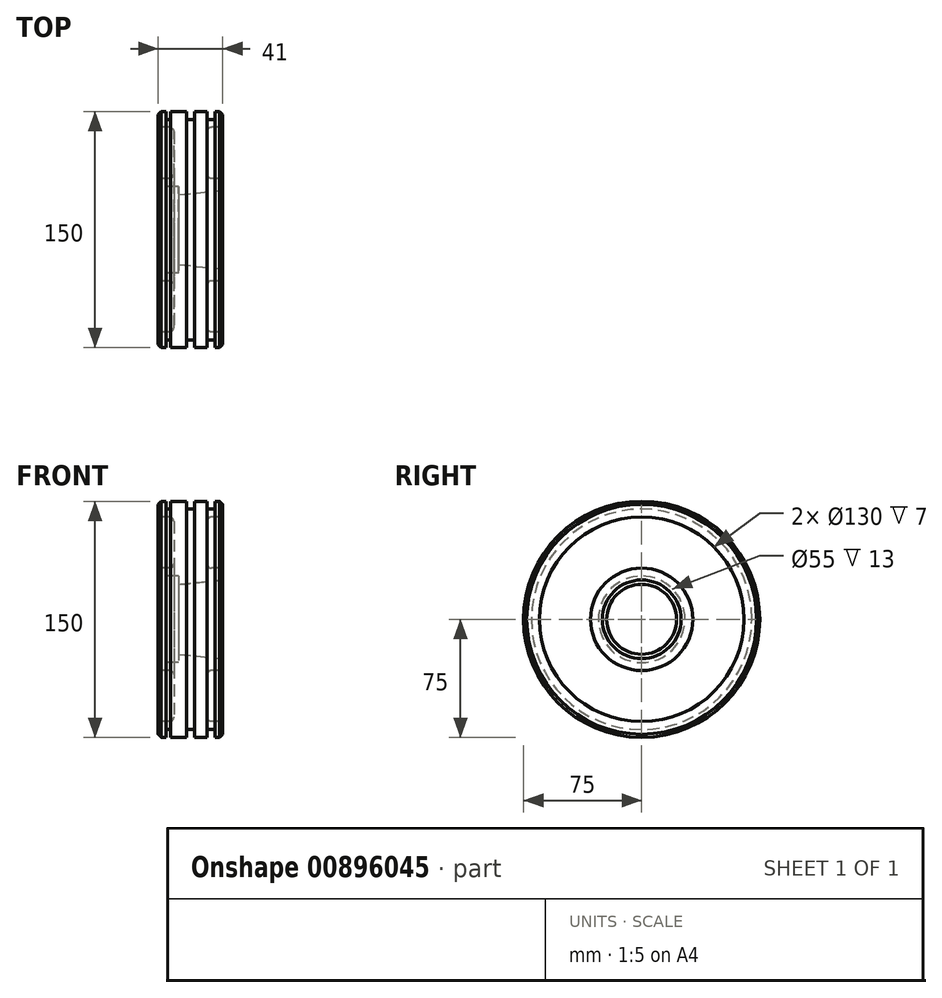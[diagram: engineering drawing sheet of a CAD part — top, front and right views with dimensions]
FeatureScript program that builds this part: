
annotation { "Feature Type Name" : "Feature", "Feature Type Description" : "" }
export const myFeature = defineFeature(function(context is Context, id is Id, definition is map)
    precondition{}
    {
        {
            var Q0;
            Q0=qCreatedBy(makeId("Front.planeOp"),FACE);
            var sketch = newSketch(context, id + "F0", { "sketchPlane" : qUnion([Q0])});
            skLineSegment(sketch, "E0", {"start": v(0, 27.5) * mm, "end": v(13, 27.5) * mm});
            skLineSegment(sketch, "E1", {"start": v(13, 27.5) * mm, "end": v(13, 22.2) * mm});
            skLineSegment(sketch, "E2", {"start": v(13, 22.2) * mm, "end": v(41, 25) * mm});
            skLineSegment(sketch, "E3", {"start": v(41, 25) * mm, "end": v(41, 32.5) * mm});
            skLineSegment(sketch, "E4", {"start": v(41, 32.5) * mm, "end": v(34, 32.5) * mm});
            skLineSegment(sketch, "E5", {"start": v(31, 35.5) * mm, "end": v(31, 62) * mm});
            skLineSegment(sketch, "E6", {"start": v(34, 65) * mm, "end": v(41, 65) * mm});
            skLineSegment(sketch, "E7", {"start": v(41, 65) * mm, "end": v(41, 75) * mm});
            skLineSegment(sketch, "E8", {"start": v(41, 75) * mm, "end": v(36, 75) * mm});
            skLineSegment(sketch, "E9", {"start": v(36, 75) * mm, "end": v(36, 70) * mm});
            skLineSegment(sketch, "E10", {"start": v(36, 70) * mm, "end": v(31, 70) * mm});
            skLineSegment(sketch, "E11", {"start": v(31, 70) * mm, "end": v(31, 75) * mm});
            skLineSegment(sketch, "E12", {"start": v(31, 75) * mm, "end": v(23, 75) * mm});
            skLineSegment(sketch, "E13", {"start": v(23, 75) * mm, "end": v(23, 70) * mm});
            skLineSegment(sketch, "E14", {"start": v(23, 70) * mm, "end": v(18, 70) * mm});
            skLineSegment(sketch, "E15", {"start": v(18, 70) * mm, "end": v(18, 75) * mm});
            skLineSegment(sketch, "E16", {"start": v(18, 75) * mm, "end": v(8, 75) * mm});
            skLineSegment(sketch, "E17", {"start": v(8, 75) * mm, "end": v(8, 70) * mm});
            skLineSegment(sketch, "E18", {"start": v(8, 70) * mm, "end": v(5, 70) * mm});
            skLineSegment(sketch, "E19", {"start": v(5, 70) * mm, "end": v(5, 75) * mm});
            skLineSegment(sketch, "E20", {"start": v(5, 75) * mm, "end": v(0, 75) * mm});
            skLineSegment(sketch, "E21", {"start": v(0, 75) * mm, "end": v(0, 65) * mm});
            skLineSegment(sketch, "E22", {"start": v(0, 65) * mm, "end": v(7, 65) * mm});
            skLineSegment(sketch, "E23", {"start": v(10, 62) * mm, "end": v(10, 35.5) * mm});
            skLineSegment(sketch, "E24", {"start": v(7, 32.5) * mm, "end": v(0, 32.5) * mm});
            skLineSegment(sketch, "E25", {"start": v(0, 32.5) * mm, "end": v(0, 27.5) * mm});
            skPoint(sketch, "E26.visualSharp", {"position": v(10, 65) * mm});
            skArc(sketch, "E26.filletArc", {"start": v(10, 62) * mm, "mid": v(9.12, 64.12) * mm, "end": v(7, 65) * mm});
            skPoint(sketch, "E27.visualSharp", {"position": v(10, 32.5) * mm});
            skArc(sketch, "E27.filletArc", {"start": v(7, 32.5) * mm, "mid": v(9.12, 33.38) * mm, "end": v(10, 35.5) * mm});
            skPoint(sketch, "E28.visualSharp", {"position": v(31, 32.5) * mm});
            skArc(sketch, "E28.filletArc", {"start": v(31, 35.5) * mm, "mid": v(31.88, 33.38) * mm, "end": v(34, 32.5) * mm});
            skPoint(sketch, "E29.visualSharp", {"position": v(31, 65) * mm});
            skArc(sketch, "E29.filletArc", {"start": v(34, 65) * mm, "mid": v(31.88, 64.12) * mm, "end": v(31, 62) * mm});
            skLineSegment(sketch, "E30", {"start": v(0, 0) * mm, "end": v(41, 0) * mm, "construction": true});
            skSolve(sketch);
        }
        {
            var Q0;
            Q0=makeQuery(id+"F0.imprint","IMPRINT",FACE,{"disambiguationData":[TD([[makeQuery(id+"F0.imprint","IMPRINT",EDGE,{"derivedFrom":sQuery(id+"F0.wireOp",EDGE,"E0")}),1.0]])]});
            var Q1;
            Q1=sQuery(id+"F0.wireOp",EDGE,"E30");
            revolve(context, id + "F1", {"surfaceOperationType" : NewSurfaceOperationType.NEW, "entities" : qUnion([Q0]), "axis" : qUnion([Q1]), "revolveType" : RevolveType.FULL});
        }
        {
            var Q0;
            Q0=makeQuery(id+"F1.opRevolve","SWEPT_EDGE",EDGE,{"disambiguationData":[OSD([sQuery(id+"F0.wireOp",EDGE,"E7"),sQuery(id+"F0.wireOp",EDGE,"E8")])]});
            var Q1;
            Q1=makeQuery(id+"F1.opRevolve","SWEPT_EDGE",EDGE,{"disambiguationData":[OSD([sQuery(id+"F0.wireOp",EDGE,"E20"),sQuery(id+"F0.wireOp",EDGE,"E21")])]});
            chamfer(context, id + "F2", {"entities" : qUnion([Q0, Q1]), "width" : 2 * mm, "tangentPropagation" : true});
        }
    });
